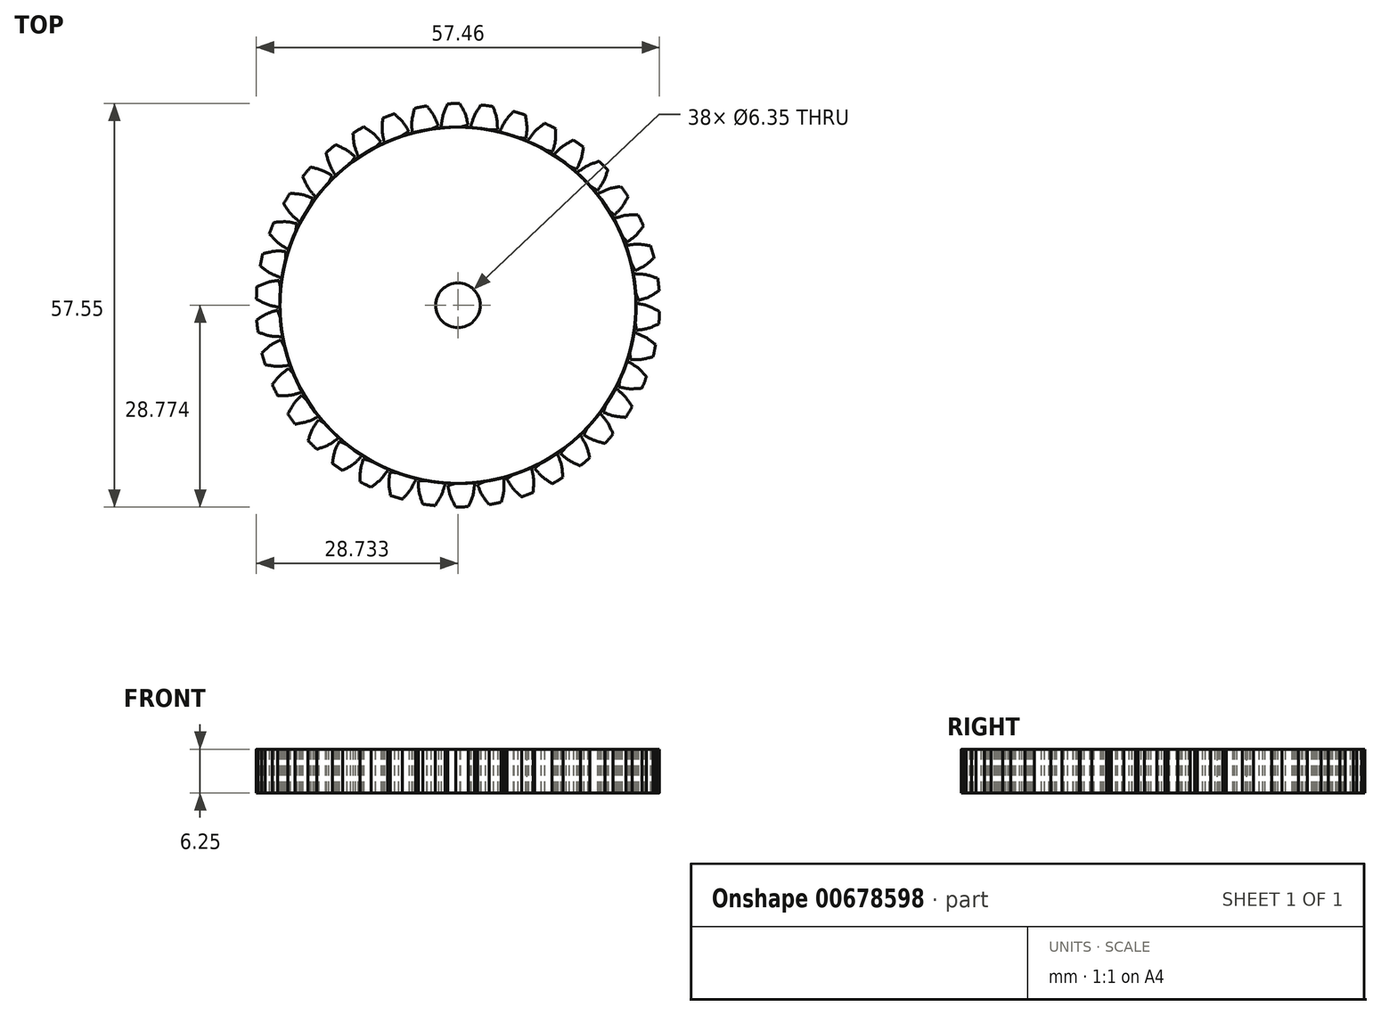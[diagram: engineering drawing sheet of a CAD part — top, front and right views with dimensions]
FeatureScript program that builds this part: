
annotation { "Feature Type Name" : "Feature", "Feature Type Description" : "" }
export const myFeature = defineFeature(function(context is Context, id is Id, definition is map)
    precondition{}
    {
        {
            var Q0;
            Q0=qCreatedBy(makeId("Top.planeOp"),FACE);
            var sketch = newSketch(context, id + "F0", { "sketchPlane" : qUnion([Q0])});
            skPoint(sketch, "E0", {"position": v(-12.24, 33.64) * mm});
            skPoint(sketch, "E1", {"position": v(0, 38.1) * mm});
            skPoint(sketch, "E2", {"position": v(-16.13, 36.62) * mm});
            skArc(sketch, "E3", {"start": v(-6.83, 40.16) * mm, "mid": v(-9.25, 39.57) * mm, "end": v(-11.63, 38.78) * mm});
            skArc(sketch, "E4", {"start": v(-11.63, 38.78) * mm, "mid": v(-13.92, 37.8) * mm, "end": v(-16.13, 36.62) * mm});
            skLineSegment(sketch, "E5", {"start": v(0.41, 36.69) * mm, "end": v(-0.74, 36.4) * mm});
            skArc(sketch, "E6.trimOffspring", {"start": v(-1.04, 36.4) * mm, "mid": v(-1.04, 36.4) * mm, "end": v(-1.04, 36.4) * mm});
            skLineSegment(sketch, "E7.0.MirrorCS", {"start": v(-3.43, 36.53) * mm, "end": v(-3.42, 36.28) * mm});
            skArc(sketch, "E8.converted", {"start": v(-3.42, 36.28) * mm, "mid": v(0, -14.38) * mm, "end": v(-0.74, 36.4) * mm});
            skLineSegment(sketch, "E9", {"start": v(-3.42, 36.28) * mm, "end": v(-3.42, 36.28) * mm});
            skArc(sketch, "E10.trimOffspring", {"start": v(-0.74, 36.4) * mm, "mid": v(-2.08, 36.36) * mm, "end": v(-3.42, 36.28) * mm});
            skArc(sketch, "E11.0", {"start": v(-0.74, 39.77) * mm, "mid": v(-1.64, 39.74) * mm, "end": v(-2.53, 39.7) * mm});
            skFitSpline(sketch, "E12.trimOffspring", {"points": [v(-2.4, 40.03) * mm, v(-3.13, 37.97) * mm, v(-3.43, 36.53) * mm], "startDerivative": vector(-1.5, -3.87) * mm, "endDerivative": vector(-0.5, -3.06) * mm});
            skFitSpline(sketch, "E13.trimOffspring", {"points": [v(-0.9, 40.1) * mm, v(0, 38.1) * mm, v(0.41, 36.69) * mm], "startDerivative": vector(1.82, -3.74) * mm, "endDerivative": vector(0.75, -3.01) * mm});
            skPoint(sketch, "E14.start.orphan", {"position": v(-0.86, 40.02) * mm});
            skPoint(sketch, "E15.trimOffspring.end.orphan", {"position": v(-2.43, 39.95) * mm});
            skCircle(sketch, "E16", {"center": v(-1.04, 11) * mm, "radius": 3.18 * mm});
            skSolve(sketch);
        }
        {
            var Q0;
            Q0=qCreatedBy(makeId("Top.planeOp"),FACE);
            var sketch = newSketch(context, id + "F1", { "sketchPlane" : qUnion([Q0])});
            skFitSpline(sketch, "E17.0", {"points": [v(-2.4, 40.03) * mm, v(-2.68, 39.32) * mm, v(-3.18, 38.02) * mm, v(-3.35, 37) * mm, v(-3.43, 36.53) * mm]});
            skFitSpline(sketch, "E18.0", {"points": [v(-0.9, 40.1) * mm, v(-0.56, 39.4) * mm, v(0.05, 38.15) * mm, v(0.3, 37.14) * mm, v(0.41, 36.69) * mm]});
            skLineSegment(sketch, "E18.1", {"start": v(0.41, 36.69) * mm, "end": v(-0.74, 36.4) * mm});
            skLineSegment(sketch, "E18.2", {"start": v(-3.43, 36.53) * mm, "end": v(-3.42, 36.28) * mm});
            skArc(sketch, "E18.3", {"start": v(-0.74, 39.77) * mm, "mid": v(-1.64, 39.74) * mm, "end": v(-2.53, 39.7) * mm});
            skArc(sketch, "E19.0", {"start": v(-3.42, 36.28) * mm, "mid": v(0, -14.38) * mm, "end": v(-0.74, 36.4) * mm});
            skSolve(sketch);
        }
        {
            var Q0;
            Q0=makeQuery(id+"F1.imprint","IMPRINT",FACE,{"disambiguationData":[TD([[makeQuery(id+"F1.imprint","IMPRINT",EDGE,{"derivedFrom":sQuery(id+"F1.wireOp",EDGE,"E17.0")}),1.0]])]});
            extrude(context, id + "F2", {"entities" : qUnion([Q0]), "depth" : 25 / 4 * mm});
        }
        {
            var Q0;
            Q0=makeQuery(id+"F2.opExtrude","CAP_FACE",FACE,{"disambiguationData":[OSD([sQuery(id+"F1.wireOp",EDGE,"E17.0"),sQuery(id+"F1.wireOp",EDGE,"E18.0"),sQuery(id+"F1.wireOp",EDGE,"E18.1"),sQuery(id+"F1.wireOp",EDGE,"E18.2"),sQuery(id+"F1.wireOp",EDGE,"E18.3"),sQuery(id+"F1.wireOp",EDGE,"E19.0")])],"isStart":false});
            var Q1;
            Q1=makeQuery(id+"F2.opExtrude","SWEPT_BODY",BODY,{"disambiguationData":[OSD([sQuery(id+"F1.wireOp",EDGE,"E17.0"),sQuery(id+"F1.wireOp",EDGE,"E18.0"),sQuery(id+"F1.wireOp",EDGE,"E18.1"),sQuery(id+"F1.wireOp",EDGE,"E18.2"),sQuery(id+"F1.wireOp",EDGE,"E18.3"),sQuery(id+"F1.wireOp",EDGE,"E19.0")])]});
            var Q2;
            Q2=sQuery(id+"F1.wireOp",EDGE,"E19.0");
            circularPattern(context, id + "F3", {"entities" : qUnion([Q1]), "axis" : qUnion([Q2]), "angle" : 360 * degree, "instanceCount" : 38, "equalSpace" : true});
        }
        {
            var Q0;
            Q0=makeQuery(id+"F0.imprint","IMPRINT",FACE,{"disambiguationData":[TD([[makeQuery(id+"F0.imprint","IMPRINT",EDGE,{"derivedFrom":sQuery(id+"F0.wireOp",EDGE,"E16")}),1.0]])]});
            extrude(context, id + "F4", {"entities" : qUnion([Q0]), "operationType" : NewBodyOperationType.REMOVE, "depth" : 6.35 * mm, "offsetDistance" : 25 * mm});
        }
    });
